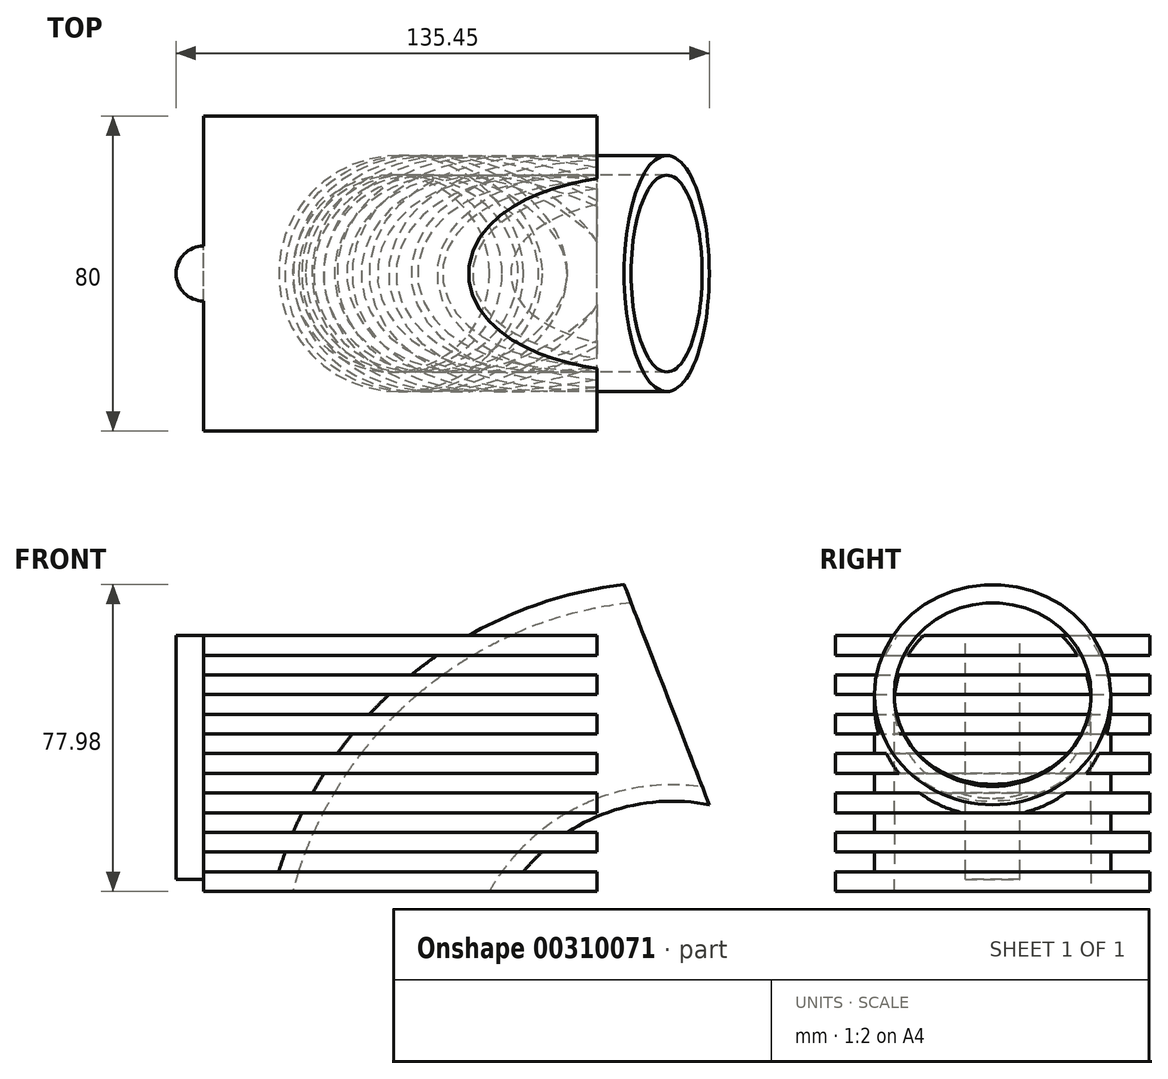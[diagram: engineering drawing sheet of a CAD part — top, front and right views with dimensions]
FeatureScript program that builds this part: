
annotation { "Feature Type Name" : "Feature", "Feature Type Description" : "" }
export const myFeature = defineFeature(function(context is Context, id is Id, definition is map)
    precondition{}
    {
        {
            var Q0;
            Q0=qCreatedBy(makeId("Top.planeOp"),FACE);
            var sketch = newSketch(context, id + "F0", { "sketchPlane" : qUnion([Q0])});
            skCircle(sketch, "E0", {"center": v(0, 0) * mm, "radius": 25 * mm});
            skCircle(sketch, "E1.0", {"center": v(0, 0) * mm, "radius": 30 * mm});
            skSolve(sketch);
        }
        {
            var Q0;
            Q0=qCreatedBy(makeId("Front.planeOp"),FACE);
            var sketch = newSketch(context, id + "F1", { "sketchPlane" : qUnion([Q0])});
            skLineSegment(sketch, "E2", {"start": v(0, 0) * mm, "end": v(70, 0) * mm});
            skLineSegment(sketch, "E3", {"start": v(70, 0) * mm, "end": v(70, 50) * mm});
            skArc(sketch, "E4", {"start": v(70, 50) * mm, "mid": v(27.26, 35.84) * mm, "end": v(0, 0) * mm});
            skSolve(sketch);
        }
        {
            var Q0;
            Q0=makeQuery(id+"F0.imprint","IMPRINT",FACE,{"disambiguationData":[TD([[makeQuery(id+"F0.imprint","IMPRINT",EDGE,{"derivedFrom":sQuery(id+"F0.wireOp",EDGE,"E0")}),-1.0]])]});
            var Q1;
            Q1=sQuery(id+"F1.wireOp",EDGE,"E4");
            sweep(context, id + "F2", {"profiles" : qUnion([Q0]), "path" : qUnion([Q1])});
        }
        {
            var Q0;
            Q0=qCreatedBy(makeId("Front.planeOp"),FACE);
            var sketch = newSketch(context, id + "F3", { "sketchPlane" : qUnion([Q0])});
            skLineSegment(sketch, "E5.bottom", {"start": v(-47.65, 5) * mm, "end": v(52.35, 5) * mm});
            skLineSegment(sketch, "E5.top", {"start": v(-47.65, 0) * mm, "end": v(52.35, 0) * mm});
            skLineSegment(sketch, "E5.left", {"start": v(-47.65, 5) * mm, "end": v(-47.65, 0) * mm});
            skLineSegment(sketch, "E5.right", {"start": v(52.35, 5) * mm, "end": v(52.35, 0) * mm});
            skLineSegment(sketch, "E6.0.1.0", {"start": v(-47.65, 15) * mm, "end": v(52.35, 15) * mm});
            skLineSegment(sketch, "E6.0.1.1", {"start": v(-47.65, 15) * mm, "end": v(-47.65, 10) * mm});
            skLineSegment(sketch, "E6.0.1.2", {"start": v(-47.65, 10) * mm, "end": v(52.35, 10) * mm});
            skLineSegment(sketch, "E6.0.1.3", {"start": v(52.35, 15) * mm, "end": v(52.35, 10) * mm});
            skLineSegment(sketch, "E6.0.2.0", {"start": v(-47.65, 25) * mm, "end": v(52.35, 25) * mm});
            skLineSegment(sketch, "E6.0.2.1", {"start": v(-47.65, 25) * mm, "end": v(-47.65, 20) * mm});
            skLineSegment(sketch, "E6.0.2.2", {"start": v(-47.65, 20) * mm, "end": v(52.35, 20) * mm});
            skLineSegment(sketch, "E6.0.2.3", {"start": v(52.35, 25) * mm, "end": v(52.35, 20) * mm});
            skLineSegment(sketch, "E6.0.3.0", {"start": v(-47.65, 35) * mm, "end": v(52.35, 35) * mm});
            skLineSegment(sketch, "E6.0.3.1", {"start": v(-47.65, 35) * mm, "end": v(-47.65, 30) * mm});
            skLineSegment(sketch, "E6.0.3.2", {"start": v(-47.65, 30) * mm, "end": v(52.35, 30) * mm});
            skLineSegment(sketch, "E6.0.3.3", {"start": v(52.35, 35) * mm, "end": v(52.35, 30) * mm});
            skLineSegment(sketch, "E6.0.4.0", {"start": v(-47.65, 45) * mm, "end": v(52.35, 45) * mm});
            skLineSegment(sketch, "E6.0.4.1", {"start": v(-47.65, 45) * mm, "end": v(-47.65, 40) * mm});
            skLineSegment(sketch, "E6.0.4.2", {"start": v(-47.65, 40) * mm, "end": v(52.35, 40) * mm});
            skLineSegment(sketch, "E6.0.4.3", {"start": v(52.35, 45) * mm, "end": v(52.35, 40) * mm});
            skLineSegment(sketch, "E6.0.5.0", {"start": v(-47.65, 55) * mm, "end": v(52.35, 55) * mm});
            skLineSegment(sketch, "E6.0.5.1", {"start": v(-47.65, 55) * mm, "end": v(-47.65, 50) * mm});
            skLineSegment(sketch, "E6.0.5.2", {"start": v(-47.65, 50) * mm, "end": v(52.35, 50) * mm});
            skLineSegment(sketch, "E6.0.5.3", {"start": v(52.35, 55) * mm, "end": v(52.35, 50) * mm});
            skLineSegment(sketch, "E6.0.6.0", {"start": v(-47.65, 65) * mm, "end": v(52.35, 65) * mm});
            skLineSegment(sketch, "E6.0.6.1", {"start": v(-47.65, 65) * mm, "end": v(-47.65, 60) * mm});
            skLineSegment(sketch, "E6.0.6.2", {"start": v(-47.65, 60) * mm, "end": v(52.35, 60) * mm});
            skLineSegment(sketch, "E6.0.6.3", {"start": v(52.35, 65) * mm, "end": v(52.35, 60) * mm});
            skLineSegment(sketch, "E6.direction1", {"start": v(-47.65, 5) * mm, "end": v(-22.65, 5) * mm, "construction": true});
            skLineSegment(sketch, "E6.direction2", {"start": v(-47.65, 5) * mm, "end": v(-47.65, 15) * mm, "construction": true});
            skSolve(sketch);
        }
        {
            var Q0;
            Q0=makeQuery(id+"F3.imprint","IMPRINT",FACE,{"disambiguationData":[TD([[makeQuery(id+"F3.imprint","IMPRINT",EDGE,{"derivedFrom":sQuery(id+"F3.wireOp",EDGE,"E6.0.6.0")}),-1.0]])]});
            var Q1;
            Q1=makeQuery(id+"F3.imprint","IMPRINT",FACE,{"disambiguationData":[TD([[makeQuery(id+"F3.imprint","IMPRINT",EDGE,{"derivedFrom":sQuery(id+"F3.wireOp",EDGE,"E6.0.5.0")}),-1.0]])]});
            var Q2;
            Q2=makeQuery(id+"F3.imprint","IMPRINT",FACE,{"disambiguationData":[TD([[makeQuery(id+"F3.imprint","IMPRINT",EDGE,{"derivedFrom":sQuery(id+"F3.wireOp",EDGE,"E6.0.4.0")}),-1.0]])]});
            var Q3;
            Q3=makeQuery(id+"F3.imprint","IMPRINT",FACE,{"disambiguationData":[TD([[makeQuery(id+"F3.imprint","IMPRINT",EDGE,{"derivedFrom":sQuery(id+"F3.wireOp",EDGE,"E6.0.3.0")}),-1.0]])]});
            var Q4;
            Q4=makeQuery(id+"F3.imprint","IMPRINT",FACE,{"disambiguationData":[TD([[makeQuery(id+"F3.imprint","IMPRINT",EDGE,{"derivedFrom":sQuery(id+"F3.wireOp",EDGE,"E6.0.2.0")}),-1.0]])]});
            var Q5;
            Q5=makeQuery(id+"F3.imprint","IMPRINT",FACE,{"disambiguationData":[TD([[makeQuery(id+"F3.imprint","IMPRINT",EDGE,{"derivedFrom":sQuery(id+"F3.wireOp",EDGE,"E6.0.1.0")}),-1.0]])]});
            var Q6;
            Q6=makeQuery(id+"F3.imprint","IMPRINT",FACE,{"disambiguationData":[TD([[makeQuery(id+"F3.imprint","IMPRINT",EDGE,{"derivedFrom":sQuery(id+"F3.wireOp",EDGE,"E5.bottom")}),-1.0]])]});
            extrude(context, id + "F4", {"entities" : qUnion([Q0, Q1, Q2, Q3, Q4, Q5, Q6]), "operationType" : NewBodyOperationType.ADD, "depth" : 40 * mm});
        }
        {
            var Q0;
            Q0=makeQuery(id+"F3.imprint","IMPRINT",FACE,{"disambiguationData":[TD([[makeQuery(id+"F3.imprint","IMPRINT",EDGE,{"derivedFrom":sQuery(id+"F3.wireOp",EDGE,"E6.0.6.0")}),-1.0]])]});
            var Q1;
            Q1=makeQuery(id+"F3.imprint","IMPRINT",FACE,{"disambiguationData":[TD([[makeQuery(id+"F3.imprint","IMPRINT",EDGE,{"derivedFrom":sQuery(id+"F3.wireOp",EDGE,"E6.0.5.0")}),-1.0]])]});
            var Q2;
            Q2=makeQuery(id+"F3.imprint","IMPRINT",FACE,{"disambiguationData":[TD([[makeQuery(id+"F3.imprint","IMPRINT",EDGE,{"derivedFrom":sQuery(id+"F3.wireOp",EDGE,"E6.0.4.0")}),-1.0]])]});
            var Q3;
            Q3=makeQuery(id+"F3.imprint","IMPRINT",FACE,{"disambiguationData":[TD([[makeQuery(id+"F3.imprint","IMPRINT",EDGE,{"derivedFrom":sQuery(id+"F3.wireOp",EDGE,"E6.0.3.0")}),-1.0]])]});
            var Q4;
            Q4=makeQuery(id+"F3.imprint","IMPRINT",FACE,{"disambiguationData":[TD([[makeQuery(id+"F3.imprint","IMPRINT",EDGE,{"derivedFrom":sQuery(id+"F3.wireOp",EDGE,"E6.0.2.0")}),-1.0]])]});
            var Q5;
            Q5=makeQuery(id+"F3.imprint","IMPRINT",FACE,{"disambiguationData":[TD([[makeQuery(id+"F3.imprint","IMPRINT",EDGE,{"derivedFrom":sQuery(id+"F3.wireOp",EDGE,"E6.0.1.0")}),-1.0]])]});
            var Q6;
            Q6=makeQuery(id+"F3.imprint","IMPRINT",FACE,{"disambiguationData":[TD([[makeQuery(id+"F3.imprint","IMPRINT",EDGE,{"derivedFrom":sQuery(id+"F3.wireOp",EDGE,"E5.bottom")}),-1.0]])]});
            extrude(context, id + "F5", {"entities" : qUnion([Q0, Q1, Q2, Q3, Q4, Q5, Q6]), "operationType" : NewBodyOperationType.ADD, "oppositeDirection" : true, "depth" : 40 * mm});
        }
        {
            var Q0;
            {var subQ0=sQuery(id+"F3.wireOp",EDGE,"E6.0.6.0");var subQ1=sQuery(id+"F3.wireOp",EDGE,"E6.0.6.1");Q0=makeQuery(id+"F5.boolean.opBoolean","MERGE",FACE,{"derivedFrom":[makeQuery(id+"F4.boolean.opBoolean","SPLIT",FACE,{"disambiguationData":[TD([makeQuery(id+"F4.opExtrude","SWEPT_FACE",FACE,{"disambiguationData":[OSD([subQ1])]})])],"derivedFrom":makeQuery(id+"F4.opExtrude","SWEPT_FACE",FACE,{"disambiguationData":[OSD([subQ0])]})}),makeQuery(id+"F5.opExtrude","SWEPT_FACE",FACE,{"disambiguationData":[OSD([subQ0])]})]});}
            var sketch = newSketch(context, id + "F6", { "sketchPlane" : qUnion([Q0])});
            skCircle(sketch, "E7", {"center": v(-47.65, 0) * mm, "radius": 6.98 * mm});
            skSolve(sketch);
        }
        {
            var Q0;
            {var subQ0=sQuery(id+"F6.wireOp",EDGE,"E7");var subQ1=sQuery(id+"F3.wireOp",EDGE,"E6.0.6.1");var subQ2=sQuery(id+"F3.wireOp",EDGE,"E6.0.6.0");var subQ3=makeQuery(id+"F5.boolean.opBoolean","MERGE",EDGE,{"derivedFrom":[makeQuery(id+"F4.opExtrude","SWEPT_EDGE",EDGE,{"disambiguationData":[OSD([subQ2,subQ1])]}),makeQuery(id+"F5.opExtrude","SWEPT_EDGE",EDGE,{"disambiguationData":[OSD([subQ2,subQ1])]})]});var subQ4=makeQuery(id+"F6.imprint","INTERSECT",VERTEX,{"disambiguationData":[OD(0.0)],"derivedFrom":[subQ3,subQ0]});Q0=makeQuery(id+"F6.imprint","IMPRINT",FACE,{"disambiguationData":[TD([[makeQuery(id+"F6.imprint","IMPRINT",EDGE,{"disambiguationData":[TD([[subQ4,1.0]])],"derivedFrom":subQ0}),1.0]])]});}
            extrude(context, id + "F7", {"entities" : qUnion([Q0]), "operationType" : NewBodyOperationType.ADD, "oppositeDirection" : true, "depth" : 62 * mm});
        }
        {
            var Q0;
            Q0=makeQuery(id+"F0.imprint","IMPRINT",FACE,{"disambiguationData":[TD([[makeQuery(id+"F0.imprint","IMPRINT",EDGE,{"derivedFrom":sQuery(id+"F0.wireOp",EDGE,"E0")}),1.0]])]});
            var Q1;
            Q1=sQuery(id+"F0.wireOp",EDGE,"E0");
            var Q2;
            Q2=sQuery(id+"F1.wireOp",EDGE,"E4");
            sweep(context, id + "F8", {"operationType" : NewBodyOperationType.REMOVE, "profiles" : qUnion([Q0]), "surfaceProfiles" : qUnion([Q1]), "path" : qUnion([Q2])});
        }
    });
